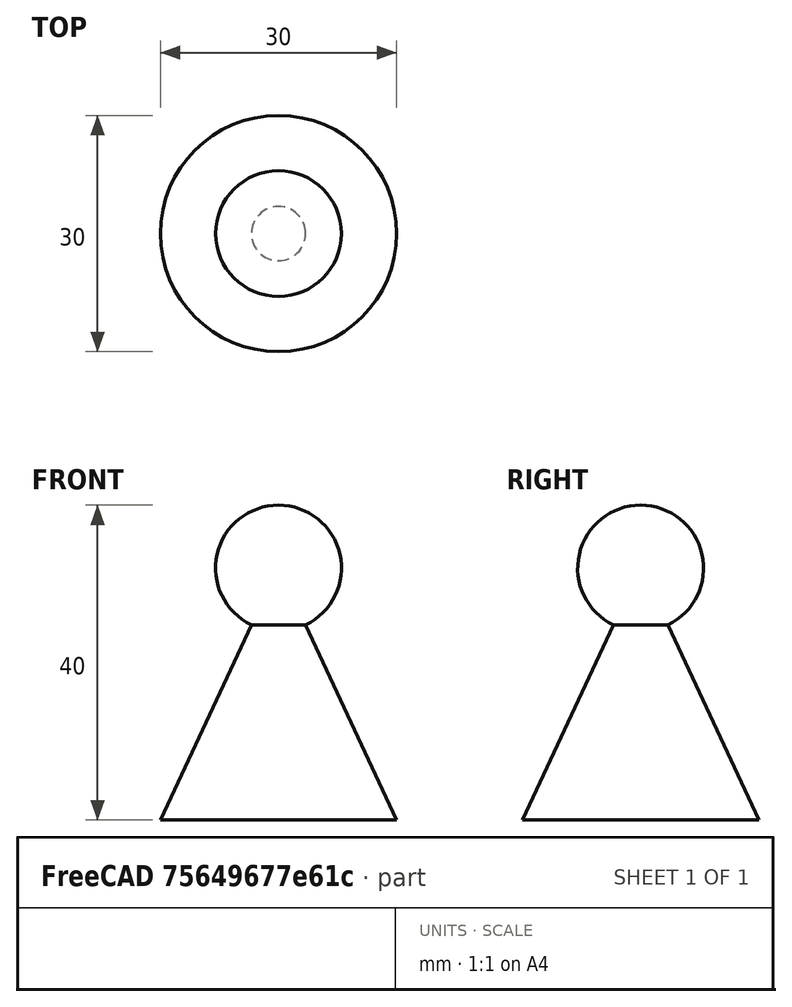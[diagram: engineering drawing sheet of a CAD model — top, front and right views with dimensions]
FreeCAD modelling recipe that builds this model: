
FCSTD DOCUMENT  (FreeCAD 0.20R29177 +233 (Git))
Label: Ficha
License: Creative Commons Attribution-ShareAlike
LicenseURL: http://creativecommons.org/licenses/by-sa/4.0/
objects: Sketcher::SketchObject×1, Part::Revolution×1
note: 2 computed .brp shape members not serialized (recipe doc carries the construction recipe); baked Part::Feature solids carry a one-line shape summary decoded from their .brp

FEATURE [Sketcher::SketchObject] Sketch
  FullyConstrained = true
  Placement = pos=(0,0,0) rot=(1,0,0;1.5708rad)
  sketch-geometry (4):
    g0: LineSegment StartX=2.4e-15 StartY=40 StartZ=0 EndX=2.4e-15 EndY=0 EndZ=0
    g1: LineSegment StartX=2.4e-15 StartY=0 StartZ=0 EndX=15 EndY=0 EndZ=0
    g2: LineSegment StartX=3.44501 StartY=24.7798 StartZ=0 EndX=15 EndY=0 EndZ=0
    g3: ArcOfCircle CenterX=0 CenterY=32 CenterZ=0 NormalX=0 NormalY=0 NormalZ=1 AngleXU=0 Radius=8 StartAngle=5.15758 EndAngle=7.85398
  constraints (12):
    c: Vertical(g0)
    c: Coincident(g0,g-1)
    c: DistanceY(g0,g0) = 40
    c: Horizontal(g1)
    c: Coincident(g1,g0)
    c: DistanceX(g1,g1) = 15
    c: Coincident(g2,g1)
    c: Angle(g2,g1) = 1.13446
    c: PointOnObject(g3,g-2)
    c: Radius(g3) = 8
    c: Coincident(g3,g0)
    c: Coincident(g3,g2)
FEATURE [Part::Revolution] Revolve
  Angle = 360
  Axis = (0,0,1)
  Base = (0,0,0)
  FaceMakerClass = Part::FaceMakerBullseye
  Solid = true
  Source = -> Sketch
  Symmetric = false
